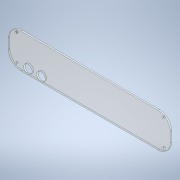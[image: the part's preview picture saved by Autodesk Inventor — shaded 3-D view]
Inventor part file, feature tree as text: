
AUTODESK INVENTOR PART (.ipt)
format: ipt  version: 2021 (Build 250183000, 183)  size: 157,696 bytes
history: native  units: mm
features: other x3, extrude x1, sketch x1
ambient origin geometry x8: Origin, YZ Plane, XZ Plane, XY Plane, X Axis, Y Axis, Z Axis, Center Point
bodies: Solid1 (feature_tree)
feature tree (5):
  other  "7 Segment Clock 3mm Walls.ipt"
  extrude  "Extrusion1"  TaperAngle=0.0deg  [1 undecoded]
  other  "FrontCover::7 Segment Clock 3mm Walls.ipt"
  other  "TaggingFeature1"
  sketch  "Sketch1"  dims[d0=10.0mm d1=0.0mm d2=0.0mm d3=0.0mm d4=0.0mm d5=0.0mm d6=0.0mm d7=0.0mm d8=0.0mm d9=0.0mm d10=0.0mm d11=0.0mm d12=0.0mm d13=0.0mm d14=0.0mm d15=0.0mm d16=0.0mm d17=0.0mm d18=0.0mm d19=0.0mm d20=0.0mm d21=0.0mm d22=2.0mm d23=0.0mm]
note: 1 required parameter value undecoded (feature->parameter linkage not recoverable at this tier; creation-order binding heuristic only, values carry confidence <= 0.55)
